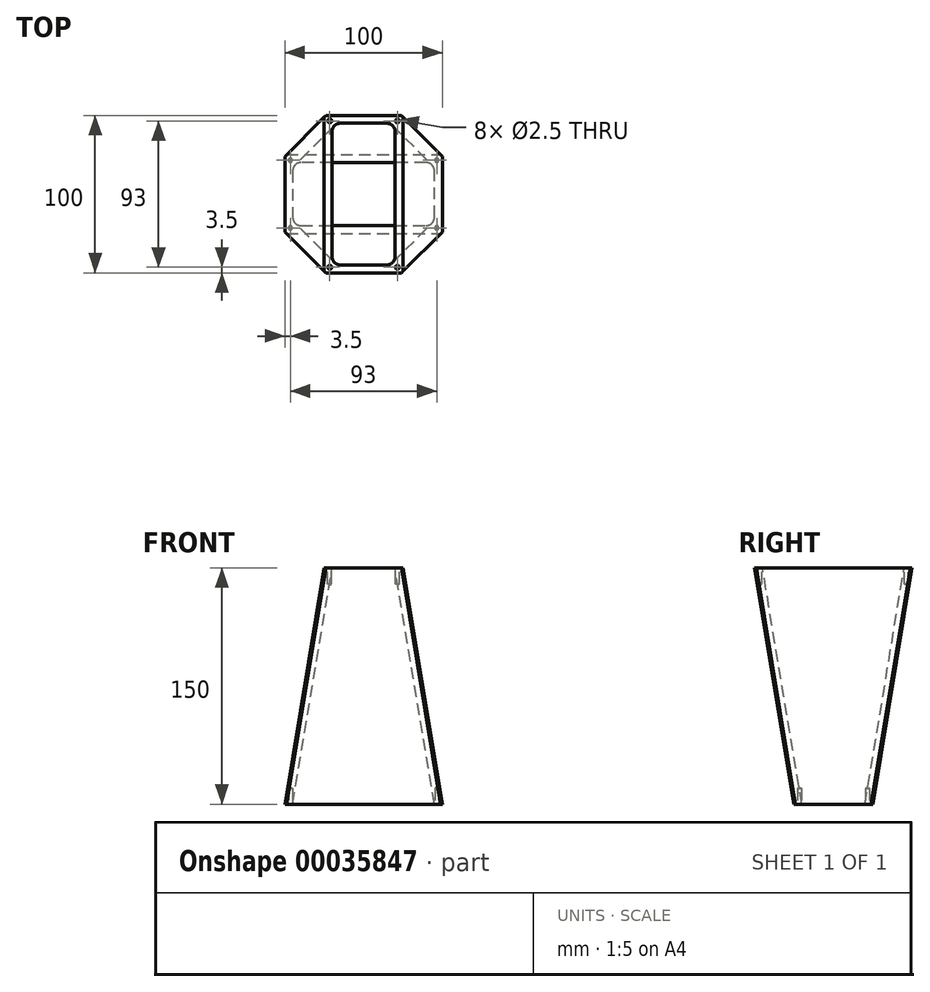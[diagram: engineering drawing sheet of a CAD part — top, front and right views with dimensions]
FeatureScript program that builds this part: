
annotation { "Feature Type Name" : "Feature", "Feature Type Description" : "" }
export const myFeature = defineFeature(function(context is Context, id is Id, definition is map)
    precondition{}
    {
        {
            var Q0;
            Q0=qCreatedBy(makeId("Top.planeOp"),FACE);
            cPlane(context, id + "F0", {"entities" : qUnion([Q0]), "cplaneType" : CPlaneType.OFFSET, "offset" : 150 * mm, "width" : 150 * mm, "height" : 150 * mm});
        }
        {
            var Q0;
            Q0=qCreatedBy(makeId("Top.planeOp"),FACE);
            var sketch = newSketch(context, id + "F1", { "sketchPlane" : qUnion([Q0])});
            skLineSegment(sketch, "E0.rect.bottom", {"start": v(-50, 25) * mm, "end": v(50, 25) * mm});
            skLineSegment(sketch, "E0.rect.top", {"start": v(-50, -25) * mm, "end": v(50, -25) * mm});
            skLineSegment(sketch, "E0.rect.left", {"start": v(-50, 25) * mm, "end": v(-50, -25) * mm});
            skLineSegment(sketch, "E0.rect.right", {"start": v(50, 25) * mm, "end": v(50, -25) * mm});
            skPoint(sketch, "E0.rect.middle", {"position": v(0, 0) * mm});
            skLineSegment(sketch, "E1", {"start": v(-46.5, 21.5) * mm, "end": v(46.5, 21.5) * mm, "construction": true});
            skLineSegment(sketch, "E2", {"start": v(46.5, 21.5) * mm, "end": v(46.5, -21.5) * mm, "construction": true});
            skLineSegment(sketch, "E3", {"start": v(46.5, -21.5) * mm, "end": v(-46.5, -21.5) * mm, "construction": true});
            skLineSegment(sketch, "E4", {"start": v(-46.5, -21.5) * mm, "end": v(-46.5, 21.5) * mm, "construction": true});
            skSolve(sketch);
        }
        {
            var Q0;
            Q0=qCreatedBy(makeId("Top.planeOp"),FACE);
            var sketch = newSketch(context, id + "F2", { "sketchPlane" : qUnion([Q0])});
            skLineSegment(sketch, "E5.0", {"start": v(45, 20) * mm, "end": v(-45, 20) * mm});
            skLineSegment(sketch, "E5.1", {"start": v(45, -20) * mm, "end": v(45, 20) * mm});
            skLineSegment(sketch, "E5.2", {"start": v(-45, -20) * mm, "end": v(45, -20) * mm});
            skLineSegment(sketch, "E5.3", {"start": v(-45, 20) * mm, "end": v(-45, -20) * mm});
            skSolve(sketch);
        }
        {
            var Q0;
            Q0=qCreatedBy(id+"F0.planeOp",FACE);
            var sketch = newSketch(context, id + "F3", { "sketchPlane" : qUnion([Q0])});
            skLineSegment(sketch, "E6.rect.bottom", {"start": v(-25, 50) * mm, "end": v(25, 50) * mm});
            skLineSegment(sketch, "E6.rect.top", {"start": v(-25, -50) * mm, "end": v(25, -50) * mm});
            skLineSegment(sketch, "E6.rect.left", {"start": v(-25, 50) * mm, "end": v(-25, -50) * mm});
            skLineSegment(sketch, "E6.rect.right", {"start": v(25, 50) * mm, "end": v(25, -50) * mm});
            skPoint(sketch, "E6.rect.middle", {"position": v(0, 0) * mm});
            skLineSegment(sketch, "E7.0", {"start": v(-21.5, 46.5) * mm, "end": v(21.5, 46.5) * mm, "construction": true});
            skLineSegment(sketch, "E8.0", {"start": v(-21.5, 46.5) * mm, "end": v(-21.5, -46.5) * mm, "construction": true});
            skLineSegment(sketch, "E9.0", {"start": v(21.5, 46.5) * mm, "end": v(21.5, -46.5) * mm, "construction": true});
            skLineSegment(sketch, "E10.0", {"start": v(-21.5, -46.5) * mm, "end": v(21.5, -46.5) * mm, "construction": true});
            skSolve(sketch);
        }
        {
            var Q0;
            Q0=qCreatedBy(id+"F0.planeOp",FACE);
            var sketch = newSketch(context, id + "F4", { "sketchPlane" : qUnion([Q0])});
            skLineSegment(sketch, "E11.0", {"start": v(20, 45) * mm, "end": v(-20, 45) * mm});
            skLineSegment(sketch, "E11.1", {"start": v(20, -45) * mm, "end": v(20, 45) * mm});
            skLineSegment(sketch, "E11.2", {"start": v(-20, -45) * mm, "end": v(20, -45) * mm});
            skLineSegment(sketch, "E11.3", {"start": v(-20, 45) * mm, "end": v(-20, -45) * mm});
            skSolve(sketch);
        }
        {
            var Q0;
            Q0 = qSketchRegion(id + "F1", true);
            var Q1;
            Q1 = qSketchRegion(id + "F3", true);
            loft(context, id + "F5", {"sheetProfilesArray" : [{ "sheetProfileEntities" : qUnion([Q0]) }, { "sheetProfileEntities" : qUnion([Q1]) }]});
        }
        {
            var Q1;
            Q1 = qSketchRegion(id + "F2", true);
            var Q2;
            Q2 = qSketchRegion(id + "F4", true);
            loft(context, id + "F6", {"operationType" : NewBodyOperationType.REMOVE, "sheetProfilesArray" : [{ "sheetProfileEntities" : qUnion([Q1]) }, { "sheetProfileEntities" : qUnion([Q2]) }]});
        }
        {
            var Q0;
            Q0=makeQuery(id+"F6.boolean.opBoolean","COPY",EDGE,{"derivedFrom":makeQuery(id+"F6.opLoft","SWEPT_EDGE",EDGE,{"disambiguationData":[OSD([sQuery(id+"F2.wireOp",EDGE,"E5.0"),sQuery(id+"F2.wireOp",EDGE,"E5.3"),sQuery(id+"F4.wireOp",EDGE,"E11.0"),sQuery(id+"F4.wireOp",EDGE,"E11.3")])]})});
            var Q1;
            Q1=makeQuery(id+"F6.boolean.opBoolean","COPY",EDGE,{"derivedFrom":makeQuery(id+"F6.opLoft","SWEPT_EDGE",EDGE,{"disambiguationData":[OSD([sQuery(id+"F2.wireOp",EDGE,"E5.0"),sQuery(id+"F2.wireOp",EDGE,"E5.1"),sQuery(id+"F4.wireOp",EDGE,"E11.0"),sQuery(id+"F4.wireOp",EDGE,"E11.1")])]})});
            var Q2;
            Q2=makeQuery(id+"F6.boolean.opBoolean","COPY",EDGE,{"derivedFrom":makeQuery(id+"F6.opLoft","SWEPT_EDGE",EDGE,{"disambiguationData":[OSD([sQuery(id+"F2.wireOp",EDGE,"E5.1"),sQuery(id+"F2.wireOp",EDGE,"E5.2"),sQuery(id+"F4.wireOp",EDGE,"E11.1"),sQuery(id+"F4.wireOp",EDGE,"E11.2")])]})});
            var Q3;
            Q3=makeQuery(id+"F6.boolean.opBoolean","COPY",EDGE,{"derivedFrom":makeQuery(id+"F6.opLoft","SWEPT_EDGE",EDGE,{"disambiguationData":[OSD([sQuery(id+"F2.wireOp",EDGE,"E5.2"),sQuery(id+"F2.wireOp",EDGE,"E5.3"),sQuery(id+"F4.wireOp",EDGE,"E11.2"),sQuery(id+"F4.wireOp",EDGE,"E11.3")])]})});
            fillet(context, id + "F7", {"entities" : qUnion([Q0, Q1, Q2, Q3]), "radius" : 5 * mm, "tangentPropagation" : true, "allowEdgeOverflow" : false});
        }
        {
            var Q0;
            Q0=makeQuery(id+"F5.opLoft","SWEPT_EDGE",EDGE,{"disambiguationData":[OSD([sQuery(id+"F1.wireOp",EDGE,"E0.rect.bottom"),sQuery(id+"F1.wireOp",EDGE,"E0.rect.right"),sQuery(id+"F3.wireOp",EDGE,"E6.rect.bottom"),sQuery(id+"F3.wireOp",EDGE,"E6.rect.right")])]});
            var Q1;
            Q1=makeQuery(id+"F5.opLoft","SWEPT_EDGE",EDGE,{"disambiguationData":[OSD([sQuery(id+"F1.wireOp",EDGE,"E0.rect.bottom"),sQuery(id+"F1.wireOp",EDGE,"E0.rect.left"),sQuery(id+"F3.wireOp",EDGE,"E6.rect.bottom"),sQuery(id+"F3.wireOp",EDGE,"E6.rect.left")])]});
            var Q2;
            Q2=makeQuery(id+"F5.opLoft","SWEPT_EDGE",EDGE,{"disambiguationData":[OSD([sQuery(id+"F1.wireOp",EDGE,"E0.rect.top"),sQuery(id+"F1.wireOp",EDGE,"E0.rect.right"),sQuery(id+"F3.wireOp",EDGE,"E6.rect.top"),sQuery(id+"F3.wireOp",EDGE,"E6.rect.right")])]});
            var Q3;
            Q3=makeQuery(id+"F5.opLoft","SWEPT_EDGE",EDGE,{"disambiguationData":[OSD([sQuery(id+"F1.wireOp",EDGE,"E0.rect.top"),sQuery(id+"F1.wireOp",EDGE,"E0.rect.left"),sQuery(id+"F3.wireOp",EDGE,"E6.rect.top"),sQuery(id+"F3.wireOp",EDGE,"E6.rect.left")])]});
            chamfer(context, id + "F8", {"entities" : qUnion([Q0, Q1, Q2, Q3]), "width" : 1 * mm, "tangentPropagation" : true});
        }
        {
            var Q0;
            Q0=sQuery(id+"F3.wireOp",VERTEX,"E9.0.start");
            var Q1;
            Q1=sQuery(id+"F3.wireOp",VERTEX,"E10.0.end");
            var Q2;
            Q2=sQuery(id+"F3.wireOp",VERTEX,"E8.0.end");
            var Q3;
            Q3=sQuery(id+"F3.wireOp",VERTEX,"E8.0.start");
            var Q4;
            Q4=makeQuery(id+"F5.opLoft","SWEPT_BODY",BODY,{"disambiguationData":[OSD([makeQuery(id+"F1.imprint","IMPRINT",FACE,{"disambiguationData":[TD([[makeQuery(id+"F1.imprint","IMPRINT",EDGE,{"derivedFrom":sQuery(id+"F1.wireOp",EDGE,"E0.rect.bottom")}),-1.0]])]}),makeQuery(id+"F3.imprint","IMPRINT",FACE,{"disambiguationData":[TD([[makeQuery(id+"F3.imprint","IMPRINT",EDGE,{"derivedFrom":sQuery(id+"F3.wireOp",EDGE,"E6.rect.bottom")}),-1.0]])]})])]});
            hole(context, id + "F9", {"style" : HoleStyle.SIMPLE, "holeDiameter" : 2.5 * mm, "endStyle" : HoleEndStyle.BLIND, "holeDepth" : 10 * mm, "locations" : qUnion([Q0, Q1, Q2, Q3]), "scope" : qUnion([Q4])});
        }
        {
            var Q0;
            Q0=sQuery(id+"F1.wireOp",VERTEX,"E2.start");
            var Q1;
            Q1=sQuery(id+"F1.wireOp",VERTEX,"E1.start");
            var Q2;
            Q2=sQuery(id+"F1.wireOp",VERTEX,"E4.start");
            var Q3;
            Q3=sQuery(id+"F1.wireOp",VERTEX,"E3.start");
            var Q4;
            Q4=makeQuery(id+"F5.opLoft","SWEPT_BODY",BODY,{"disambiguationData":[OSD([makeQuery(id+"F1.imprint","IMPRINT",FACE,{"disambiguationData":[TD([[makeQuery(id+"F1.imprint","IMPRINT",EDGE,{"derivedFrom":sQuery(id+"F1.wireOp",EDGE,"E0.rect.bottom")}),-1.0]])]}),makeQuery(id+"F3.imprint","IMPRINT",FACE,{"disambiguationData":[TD([[makeQuery(id+"F3.imprint","IMPRINT",EDGE,{"derivedFrom":sQuery(id+"F3.wireOp",EDGE,"E6.rect.bottom")}),-1.0]])]})])]});
            hole(context, id + "F10", {"style" : HoleStyle.SIMPLE, "holeDiameter" : 2.5 * mm, "endStyle" : HoleEndStyle.BLIND, "oppositeDirection" : true, "holeDepth" : 10 * mm, "locations" : qUnion([Q0, Q1, Q2, Q3]), "scope" : qUnion([Q4])});
        }
    });
